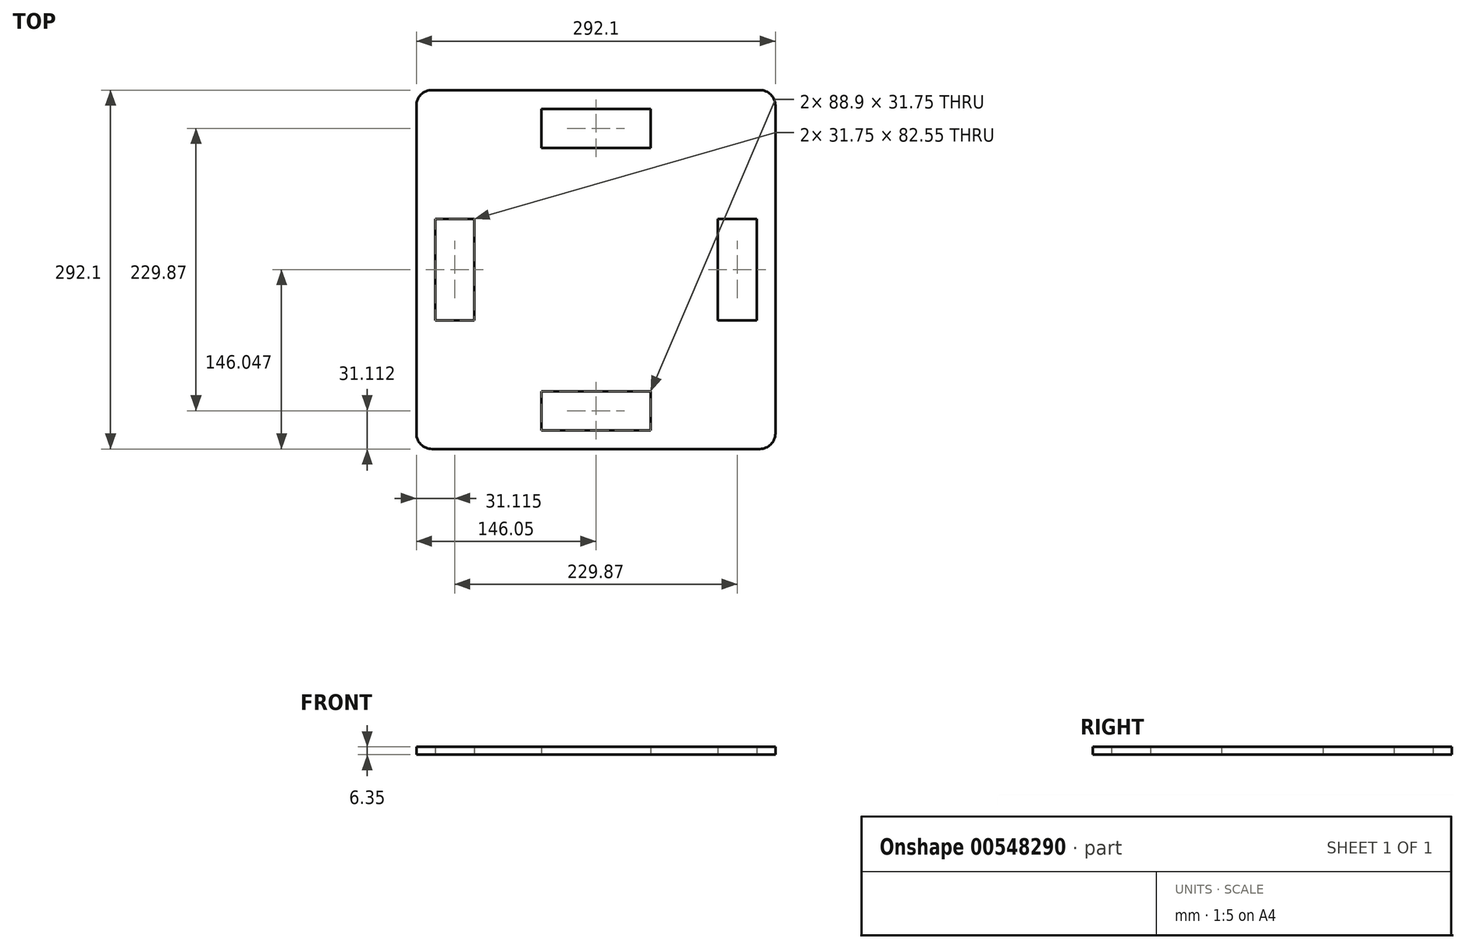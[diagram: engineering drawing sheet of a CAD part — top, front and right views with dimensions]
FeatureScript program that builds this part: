
annotation { "Feature Type Name" : "Feature", "Feature Type Description" : "" }
export const myFeature = defineFeature(function(context is Context, id is Id, definition is map)
    precondition{}
    {
        {
            var Q0;
            Q0=qCreatedBy(makeId("Top.planeOp"),FACE);
            var sketch = newSketch(context, id + "F0", { "sketchPlane" : qUnion([Q0])});
            skLineSegment(sketch, "E0.bottom", {"start": v(-133.35, -137.14) * mm, "end": v(133.35, -137.14) * mm});
            skLineSegment(sketch, "E0.top", {"start": v(-133.35, 154.96) * mm, "end": v(133.35, 154.96) * mm});
            skLineSegment(sketch, "E0.left", {"start": v(-146.05, -124.44) * mm, "end": v(-146.05, 142.26) * mm});
            skLineSegment(sketch, "E0.right", {"start": v(146.05, -124.44) * mm, "end": v(146.05, 142.26) * mm});
            skPoint(sketch, "E1.visualSharp", {"position": v(-146.05, 154.96) * mm});
            skArc(sketch, "E1.filletArc", {"start": v(-133.35, 154.96) * mm, "mid": v(-142.33, 151.24) * mm, "end": v(-146.05, 142.26) * mm});
            skPoint(sketch, "E2.visualSharp", {"position": v(146.05, 154.96) * mm});
            skArc(sketch, "E2.filletArc", {"start": v(146.05, 142.26) * mm, "mid": v(142.33, 151.24) * mm, "end": v(133.35, 154.96) * mm});
            skPoint(sketch, "E3.visualSharp", {"position": v(146.05, -137.14) * mm});
            skArc(sketch, "E3.filletArc", {"start": v(133.35, -137.14) * mm, "mid": v(142.33, -133.42) * mm, "end": v(146.05, -124.44) * mm});
            skPoint(sketch, "E4.visualSharp", {"position": v(-146.05, -137.14) * mm});
            skArc(sketch, "E4.filletArc", {"start": v(-146.05, -124.44) * mm, "mid": v(-142.33, -133.42) * mm, "end": v(-133.35, -137.14) * mm});
            skLineSegment(sketch, "E5", {"start": v(-146.05, 8.9) * mm, "end": v(146.05, 8.9) * mm, "construction": true});
            skLineSegment(sketch, "E6", {"start": v(0, 154.96) * mm, "end": v(0, -137.14) * mm, "construction": true});
            skLineSegment(sketch, "E7.bottom", {"start": v(44.45, 139.72) * mm, "end": v(-44.45, 139.72) * mm});
            skLineSegment(sketch, "E7.top", {"start": v(44.45, 107.97) * mm, "end": v(-44.45, 107.97) * mm});
            skLineSegment(sketch, "E7.left", {"start": v(44.45, 139.72) * mm, "end": v(44.45, 107.97) * mm});
            skLineSegment(sketch, "E7.right", {"start": v(-44.45, 139.72) * mm, "end": v(-44.45, 107.97) * mm});
            skPoint(sketch, "E7.middle", {"position": v(0, 123.84) * mm});
            skLineSegment(sketch, "E8.MirrorCS", {"start": v(44.45, -121.9) * mm, "end": v(-44.45, -121.9) * mm});
            skLineSegment(sketch, "E9.MirrorCS", {"start": v(-44.45, -121.9) * mm, "end": v(-44.45, -90.15) * mm});
            skLineSegment(sketch, "E10.MirrorCS", {"start": v(44.45, -90.15) * mm, "end": v(-44.45, -90.15) * mm});
            skLineSegment(sketch, "E11.MirrorCS", {"start": v(44.45, -121.9) * mm, "end": v(44.45, -90.15) * mm});
            skLineSegment(sketch, "E12.bottom", {"start": v(-99.06, 50.18) * mm, "end": v(-130.8, 50.18) * mm});
            skLineSegment(sketch, "E12.top", {"start": v(-99.06, -32.37) * mm, "end": v(-130.8, -32.37) * mm});
            skLineSegment(sketch, "E12.left", {"start": v(-99.06, 50.18) * mm, "end": v(-99.06, -32.37) * mm});
            skLineSegment(sketch, "E12.right", {"start": v(-130.8, 50.18) * mm, "end": v(-130.8, -32.37) * mm});
            skPoint(sketch, "E12.middle", {"position": v(-114.94, 8.9) * mm});
            skLineSegment(sketch, "E13.MirrorCS", {"start": v(99.06, 50.18) * mm, "end": v(99.06, -32.37) * mm});
            skLineSegment(sketch, "E14.MirrorCS", {"start": v(99.06, 50.18) * mm, "end": v(130.81, 50.18) * mm});
            skLineSegment(sketch, "E15.MirrorCS", {"start": v(130.8, 50.18) * mm, "end": v(130.81, -32.37) * mm});
            skLineSegment(sketch, "E16.MirrorCS", {"start": v(99.06, -32.37) * mm, "end": v(130.81, -32.37) * mm});
            skSolve(sketch);
        }
        {
            var Q0;
            Q0 = qSketchRegion(id + "F0", true);
            extrude(context, id + "F1", {"entities" : qUnion([Q0]), "depth" : 6.35 * mm, "offsetDistance" : 25.4 * mm});
        }
    });
